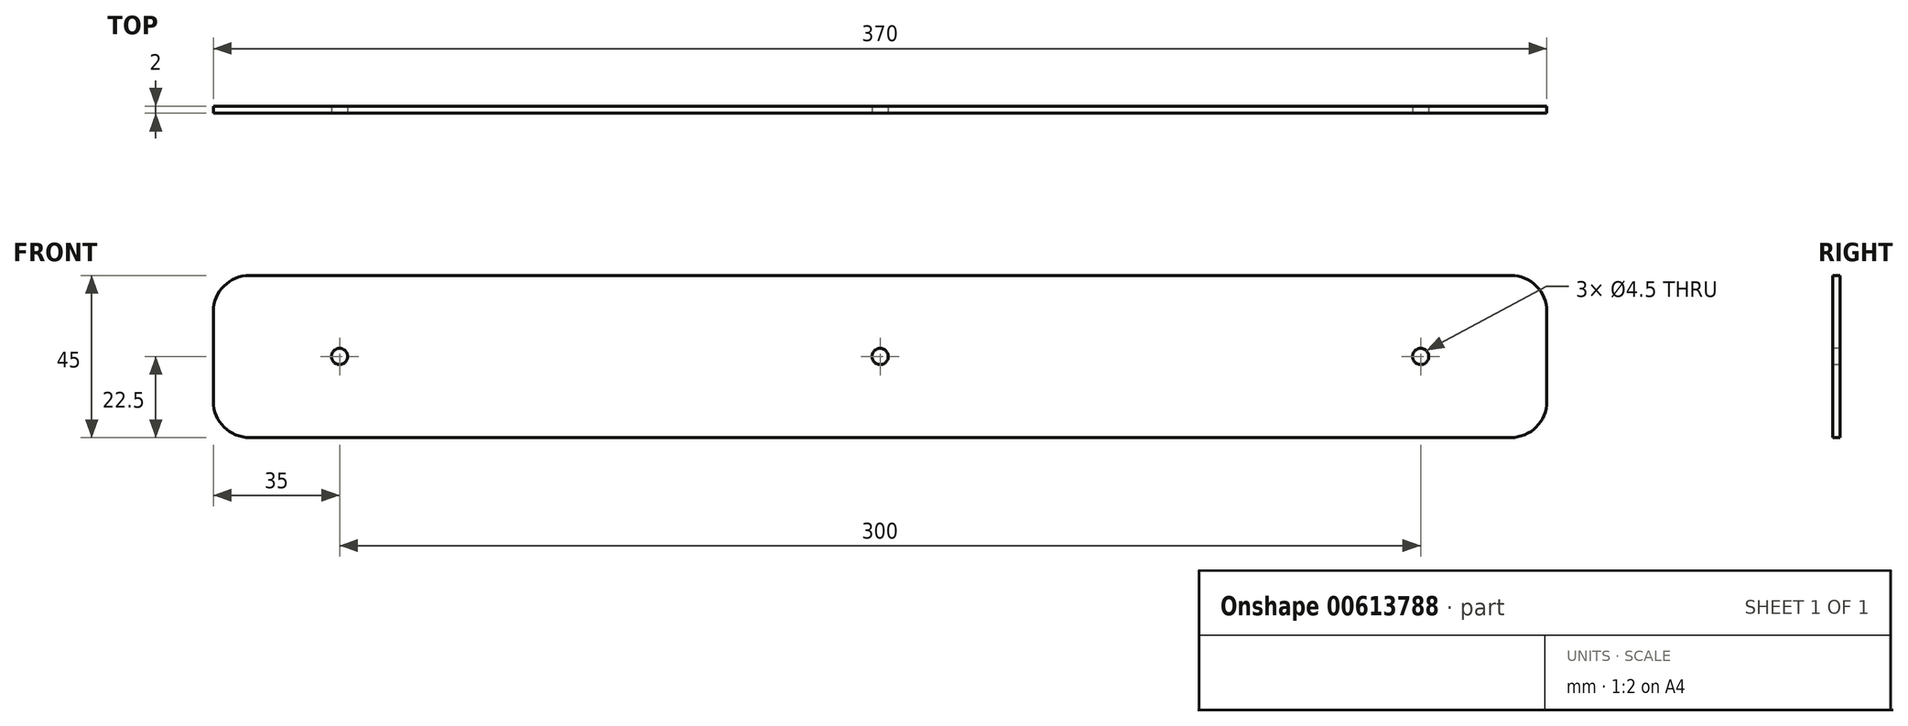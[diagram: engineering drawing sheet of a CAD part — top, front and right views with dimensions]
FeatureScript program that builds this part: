
annotation { "Feature Type Name" : "Feature", "Feature Type Description" : "" }
export const myFeature = defineFeature(function(context is Context, id is Id, definition is map)
    precondition{}
    {
        {
            var Q0;
            Q0=qCreatedBy(makeId("Front.planeOp"),FACE);
            var sketch = newSketch(context, id + "F0", { "sketchPlane" : qUnion([Q0])});
            skLineSegment(sketch, "E0.bottom", {"start": v(-185, 0) * mm, "end": v(185, 0) * mm});
            skLineSegment(sketch, "E0.top", {"start": v(-185, 45) * mm, "end": v(185, 45) * mm});
            skLineSegment(sketch, "E0.left", {"start": v(-185, 0) * mm, "end": v(-185, 45) * mm});
            skLineSegment(sketch, "E0.right", {"start": v(185, 0) * mm, "end": v(185, 45) * mm});
            skSolve(sketch);
        }
        {
            var Q0;
            Q0=makeQuery(id+"F0.imprint","IMPRINT",FACE,{"disambiguationData":[TD([[makeQuery(id+"F0.imprint","IMPRINT",EDGE,{"derivedFrom":sQuery(id+"F0.wireOp",EDGE,"E0.bottom")}),1.0]])]});
            extrude(context, id + "F1", {"entities" : qUnion([Q0]), "depth" : 2 * mm, "offsetDistance" : 25 * mm});
        }
        {
            var Q0;
            Q0=makeQuery(id+"F1.opExtrude","CAP_FACE",FACE,{"disambiguationData":[OSD([sQuery(id+"F0.wireOp",EDGE,"E0.bottom"),sQuery(id+"F0.wireOp",EDGE,"E0.top"),sQuery(id+"F0.wireOp",EDGE,"E0.left"),sQuery(id+"F0.wireOp",EDGE,"E0.right")])],"isStart":false});
            var sketch = newSketch(context, id + "F2", { "sketchPlane" : qUnion([Q0])});
            skLineSegment(sketch, "E1", {"start": v(-150, 22.5) * mm, "end": v(150, 22.5) * mm, "construction": true});
            skPoint(sketch, "E2.endSnap0", {"position": v(0, 22.5) * mm});
            skCircle(sketch, "E3", {"center": v(0, 22.5) * mm, "radius": 2.25 * mm});
            skCircle(sketch, "E4", {"center": v(-150, 22.5) * mm, "radius": 2.25 * mm});
            skCircle(sketch, "E5", {"center": v(150, 22.5) * mm, "radius": 2.25 * mm});
            skSolve(sketch);
        }
        {
            var Q0;
            Q0=qSketchRegion(id+"F2",true);
            extrude(context, id + "F3", {"entities" : qUnion([Q0]), "operationType" : NewBodyOperationType.REMOVE, "oppositeDirection" : true, "depth" : 25 * mm, "offsetDistance" : 25 * mm});
        }
        {
            var Q0;
            Q0=makeQuery(id+"F1.opExtrude","SWEPT_EDGE",EDGE,{"disambiguationData":[OSD([sQuery(id+"F0.wireOp",EDGE,"E0.top"),sQuery(id+"F0.wireOp",EDGE,"E0.right")])]});
            var Q1;
            Q1=makeQuery(id+"F1.opExtrude","SWEPT_EDGE",EDGE,{"disambiguationData":[OSD([sQuery(id+"F0.wireOp",EDGE,"E0.bottom"),sQuery(id+"F0.wireOp",EDGE,"E0.right")])]});
            var Q2;
            Q2=makeQuery(id+"F1.opExtrude","SWEPT_EDGE",EDGE,{"disambiguationData":[OSD([sQuery(id+"F0.wireOp",EDGE,"E0.top"),sQuery(id+"F0.wireOp",EDGE,"E0.left")])]});
            var Q3;
            Q3=makeQuery(id+"F1.opExtrude","SWEPT_EDGE",EDGE,{"disambiguationData":[OSD([sQuery(id+"F0.wireOp",EDGE,"E0.bottom"),sQuery(id+"F0.wireOp",EDGE,"E0.left")])]});
            fillet(context, id + "F4", {"entities" : qUnion([Q0, Q1, Q2, Q3]), "radius" : 10 * mm, "tangentPropagation" : true, "allowEdgeOverflow" : false});
        }
    });
